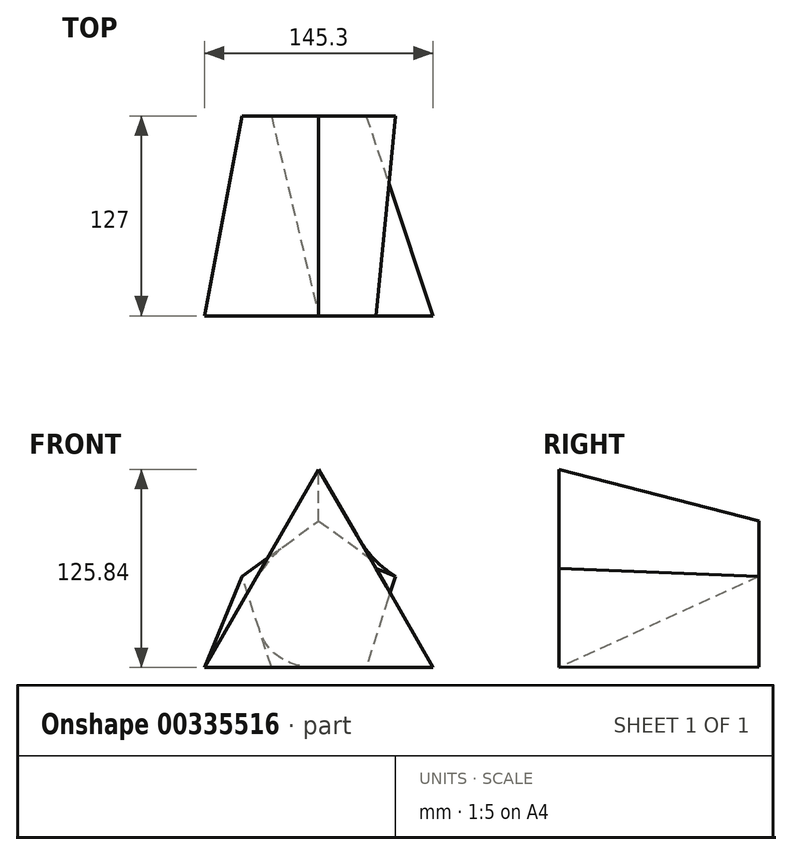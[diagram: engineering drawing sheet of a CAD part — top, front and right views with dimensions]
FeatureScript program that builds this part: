
annotation { "Feature Type Name" : "Feature", "Feature Type Description" : "" }
export const myFeature = defineFeature(function(context is Context, id is Id, definition is map)
    precondition{}
    {
        {
            var Q0;
            Q0=qCreatedBy(makeId("Front.planeOp"),FACE);
            var sketch = newSketch(context, id + "F0", { "sketchPlane" : qUnion([Q0])});
            skCircle(sketch, "E0.cCircle", {"center": v(0, 0) * mm, "radius": 41.43 * mm, "construction": true});
            skLineSegment(sketch, "E0.0", {"start": v(30.1, -41.43) * mm, "end": v(-30.1, -41.43) * mm});
            skLineSegment(sketch, "E0.1", {"start": v(-30.1, -41.43) * mm, "end": v(-48.7, 15.83) * mm});
            skLineSegment(sketch, "E0.2", {"start": v(-48.7, 15.83) * mm, "end": v(0, 51.21) * mm});
            skLineSegment(sketch, "E0.3", {"start": v(0, 51.21) * mm, "end": v(48.7, 15.83) * mm});
            skLineSegment(sketch, "E0.4", {"start": v(48.7, 15.83) * mm, "end": v(30.1, -41.43) * mm});
            skPoint(sketch, "E0.0.midPoint", {"position": v(0, -41.43) * mm});
            skSolve(sketch);
        }
        {
            var Q0;
            Q0=makeQuery(id+"F0.imprint","IMPRINT",FACE,{"disambiguationData":[TD([[makeQuery(id+"F0.imprint","IMPRINT",EDGE,{"derivedFrom":sQuery(id+"F0.wireOp",EDGE,"E0.0")}),-1.0]])]});
            cPlane(context, id + "F1", {"entities" : qUnion([Q0]), "cplaneType" : CPlaneType.OFFSET, "offset" : 127 * mm, "width" : 152.4 * mm, "height" : 152.4 * mm});
        }
        {
            var Q0;
            Q0=qCreatedBy(id+"F1.planeOp",FACE);
            var sketch = newSketch(context, id + "F2", { "sketchPlane" : qUnion([Q0])});
            skCircle(sketch, "E1.cCircle", {"center": v(0, 0) * mm, "radius": 41.95 * mm, "construction": true});
            skLineSegment(sketch, "E1.0", {"start": v(72.65, -41.95) * mm, "end": v(-72.65, -41.95) * mm});
            skLineSegment(sketch, "E1.1", {"start": v(-72.65, -41.95) * mm, "end": v(0, 83.9) * mm});
            skLineSegment(sketch, "E1.2", {"start": v(0, 83.9) * mm, "end": v(72.65, -41.95) * mm});
            skPoint(sketch, "E1.0.midPoint", {"position": v(0, -41.95) * mm});
            skSolve(sketch);
        }
        {
            var Q0;
            Q0 = qSketchRegion(id + "F0", true);
            var Q1;
            Q1 = qSketchRegion(id + "F2", true);
            loft(context, id + "F3", {"sheetProfilesArray" : [{ "sheetProfileEntities" : qUnion([Q0]) }, { "sheetProfileEntities" : qUnion([Q1]) }]});
        }
    });
